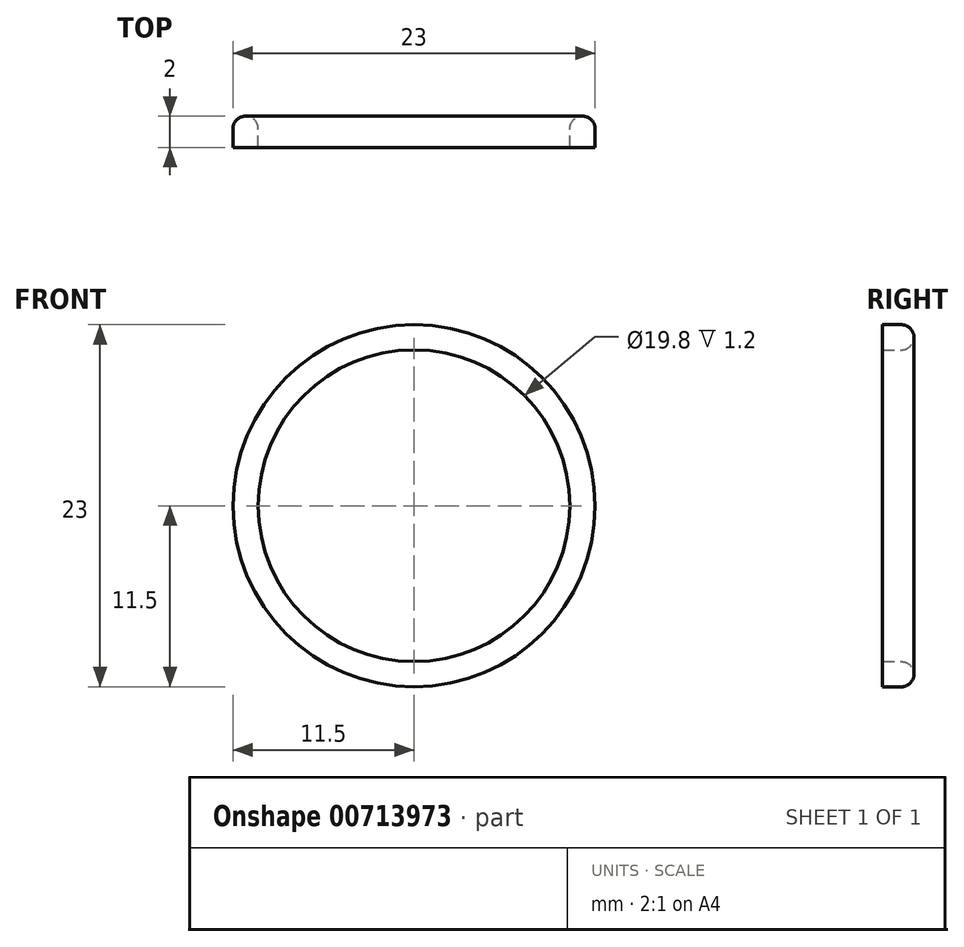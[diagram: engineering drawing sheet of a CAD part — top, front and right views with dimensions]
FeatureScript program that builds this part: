
annotation { "Feature Type Name" : "Feature", "Feature Type Description" : "" }
export const myFeature = defineFeature(function(context is Context, id is Id, definition is map)
    precondition{}
    {
        {
            var Q0;
            Q0=qCreatedBy(makeId("Front.planeOp"),FACE);
            var sketch = newSketch(context, id + "F0", { "sketchPlane" : qUnion([Q0])});
            skCircle(sketch, "E0", {"center": v(0, 0) * mm, "radius": 9.9 * mm});
            skCircle(sketch, "E1.0", {"center": v(0, 0) * mm, "radius": 11.5 * mm});
            skSolve(sketch);
        }
        {
            var Q0;
            Q0=makeQuery(id+"F0.imprint","IMPRINT",FACE,{"disambiguationData":[TD([[makeQuery(id+"F0.imprint","IMPRINT",EDGE,{"derivedFrom":sQuery(id+"F0.wireOp",EDGE,"E0")}),-1.0]])]});
            extrude(context, id + "F1", {"entities" : qUnion([Q0]), "depth" : 2 * mm, "offsetDistance" : 25 * mm});
        }
        {
            var Q0;
            Q0=makeQuery(id+"F1.opExtrude","CAP_EDGE",EDGE,{"disambiguationData":[OSD([sQuery(id+"F0.wireOp",EDGE,"E1.0")])],"isStart":true});
            var Q1;
            Q1=makeQuery(id+"F1.opExtrude","CAP_EDGE",EDGE,{"disambiguationData":[OSD([sQuery(id+"F0.wireOp",EDGE,"E0")])],"isStart":true});
            fillet(context, id + "F2", {"entities" : qUnion([Q0, Q1]), "radius" : 0.8 * mm, "tangentPropagation" : true, "allowEdgeOverflow" : false});
        }
    });
